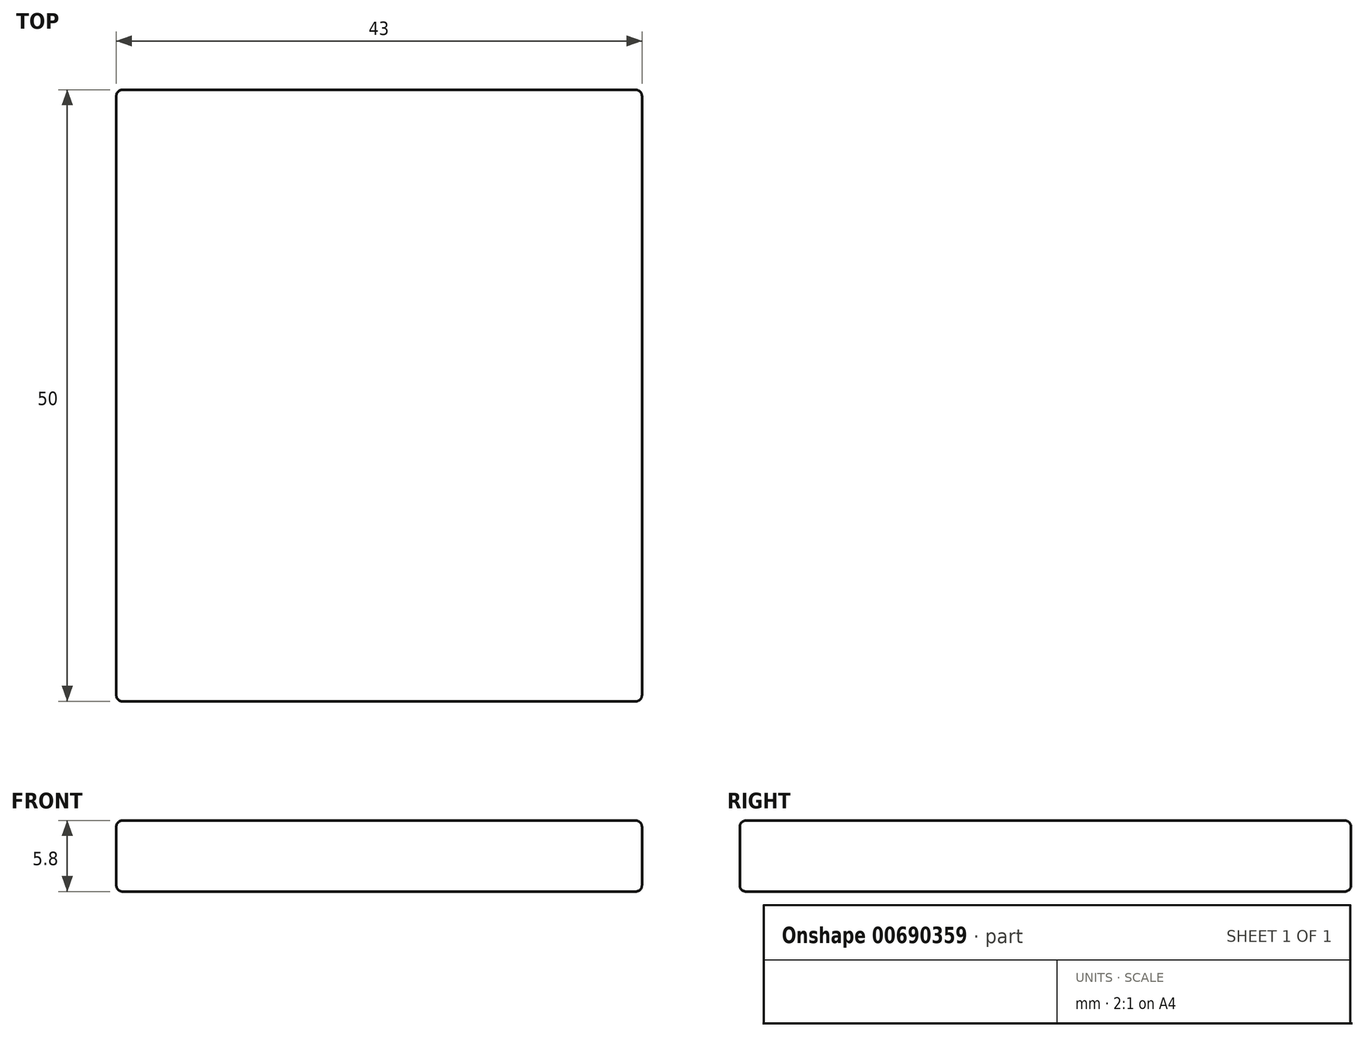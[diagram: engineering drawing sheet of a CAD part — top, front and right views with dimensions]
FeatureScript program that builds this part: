
annotation { "Feature Type Name" : "Feature", "Feature Type Description" : "" }
export const myFeature = defineFeature(function(context is Context, id is Id, definition is map)
    precondition{}
    {
        {
            var Q0;
            Q0=qCreatedBy(makeId("Top.planeOp"),FACE);
            var sketch = newSketch(context, id + "F0", { "sketchPlane" : qUnion([Q0])});
            skLineSegment(sketch, "E0.bottom", {"start": v(21.5, 25) * mm, "end": v(-21.5, 25) * mm});
            skLineSegment(sketch, "E0.top", {"start": v(21.5, -25) * mm, "end": v(-21.5, -25) * mm});
            skLineSegment(sketch, "E0.left", {"start": v(21.5, 25) * mm, "end": v(21.5, -25) * mm});
            skLineSegment(sketch, "E0.right", {"start": v(-21.5, 25) * mm, "end": v(-21.5, -25) * mm});
            skPoint(sketch, "E0.middle", {"position": v(0, 0) * mm});
            skSolve(sketch);
        }
        {
            var Q0;
            Q0=makeQuery(id+"F0.imprint","IMPRINT",FACE,{"disambiguationData":[TD([[makeQuery(id+"F0.imprint","IMPRINT",EDGE,{"derivedFrom":sQuery(id+"F0.wireOp",EDGE,"E0.bottom")}),1.0]])]});
            extrude(context, id + "F1", {"entities" : qUnion([Q0]), "depth" : 5.8 * mm, "offsetDistance" : 25 * mm});
        }
        {
            var Q0;
            Q0=makeQuery(id+"F1.opExtrude","SWEPT_EDGE",EDGE,{"disambiguationData":[OSD([sQuery(id+"F0.wireOp",EDGE,"E0.top"),sQuery(id+"F0.wireOp",EDGE,"E0.left")])]});
            var Q1;
            Q1=makeQuery(id+"F1.opExtrude","SWEPT_EDGE",EDGE,{"disambiguationData":[OSD([sQuery(id+"F0.wireOp",EDGE,"E0.top"),sQuery(id+"F0.wireOp",EDGE,"E0.right")])]});
            var Q2;
            Q2=makeQuery(id+"F1.opExtrude","SWEPT_EDGE",EDGE,{"disambiguationData":[OSD([sQuery(id+"F0.wireOp",EDGE,"E0.bottom"),sQuery(id+"F0.wireOp",EDGE,"E0.left")])]});
            var Q3;
            Q3=makeQuery(id+"F1.opExtrude","SWEPT_EDGE",EDGE,{"disambiguationData":[OSD([sQuery(id+"F0.wireOp",EDGE,"E0.bottom"),sQuery(id+"F0.wireOp",EDGE,"E0.right")])]});
            var Q4;
            Q4=makeQuery(id+"F1.opExtrude","CAP_FACE",FACE,{"disambiguationData":[OSD([sQuery(id+"F0.wireOp",EDGE,"E0.bottom"),sQuery(id+"F0.wireOp",EDGE,"E0.top"),sQuery(id+"F0.wireOp",EDGE,"E0.left"),sQuery(id+"F0.wireOp",EDGE,"E0.right")])],"isStart":false});
            var Q5;
            Q5=makeQuery(id+"F1.opExtrude","CAP_FACE",FACE,{"disambiguationData":[OSD([sQuery(id+"F0.wireOp",EDGE,"E0.bottom"),sQuery(id+"F0.wireOp",EDGE,"E0.top"),sQuery(id+"F0.wireOp",EDGE,"E0.left"),sQuery(id+"F0.wireOp",EDGE,"E0.right")])],"isStart":true});
            fillet(context, id + "F2", {"entities" : qUnion([Q0, Q1, Q2, Q3, Q4, Q5]), "radius" : 0.5 * mm, "tangentPropagation" : true, "allowEdgeOverflow" : false});
        }
    });
